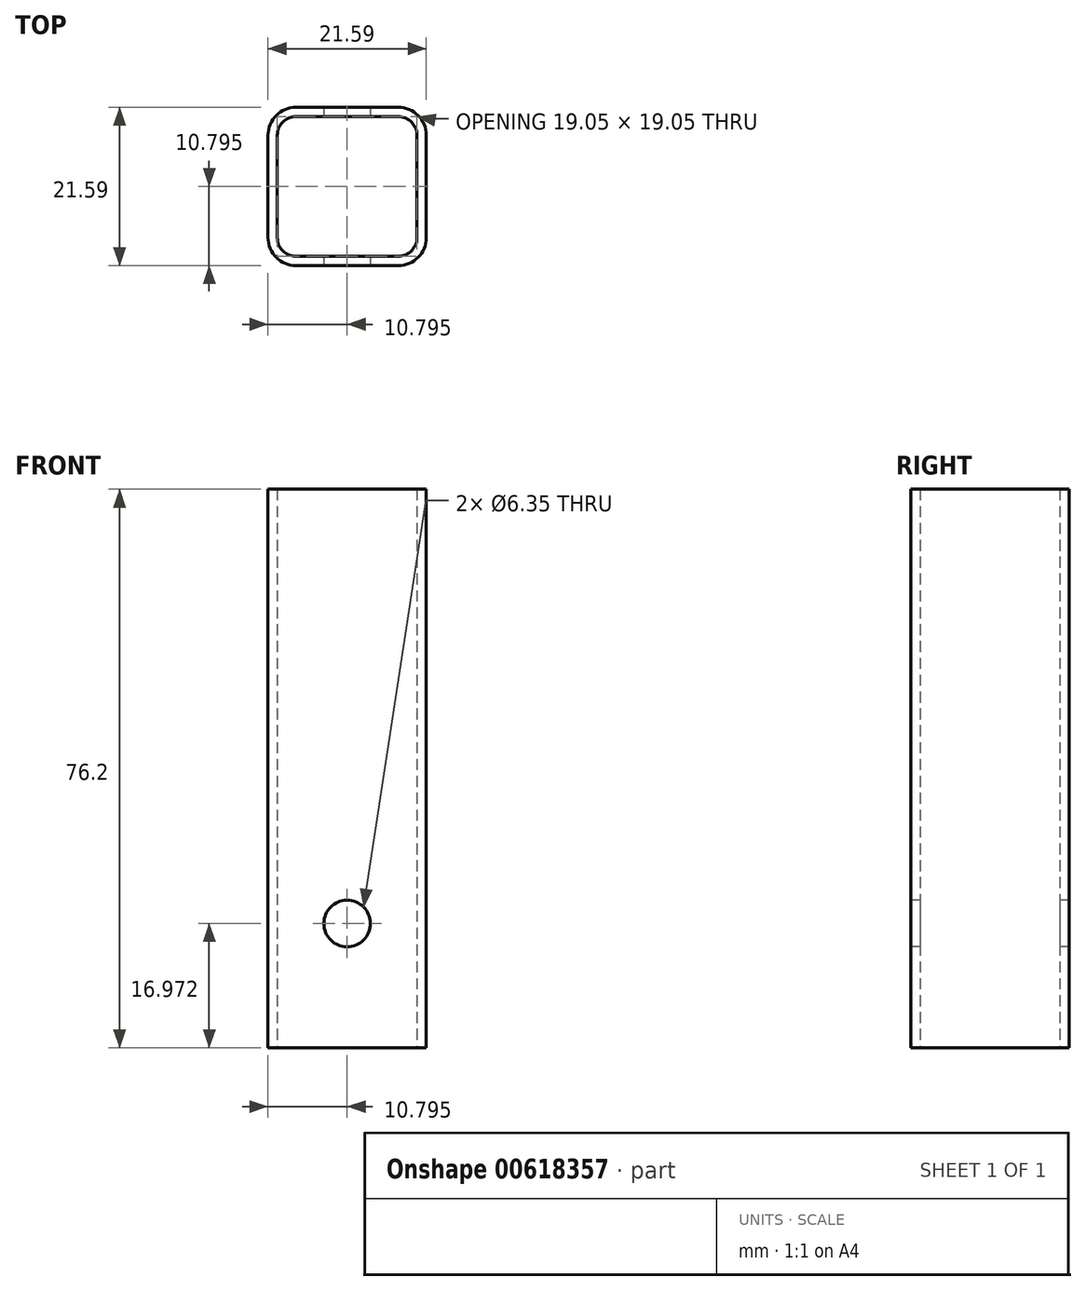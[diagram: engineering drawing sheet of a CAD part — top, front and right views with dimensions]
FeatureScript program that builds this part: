
annotation { "Feature Type Name" : "Feature", "Feature Type Description" : "" }
export const myFeature = defineFeature(function(context is Context, id is Id, definition is map)
    precondition{}
    {
        {
            var Q0;
            Q0=qCreatedBy(makeId("Top.planeOp"),FACE);
            var sketch = newSketch(context, id + "F0", { "sketchPlane" : qUnion([Q0])});
            skLineSegment(sketch, "E0.bottom", {"start": v(2.54, 0) * mm, "end": v(16.51, 0) * mm});
            skLineSegment(sketch, "E0.top", {"start": v(2.54, 19.05) * mm, "end": v(16.5, 19.05) * mm});
            skLineSegment(sketch, "E0.left", {"start": v(0, 2.54) * mm, "end": v(0, 16.5) * mm});
            skLineSegment(sketch, "E0.right", {"start": v(19.05, 2.54) * mm, "end": v(19.05, 16.51) * mm});
            skPoint(sketch, "E1.visualSharp", {"position": v(0, 19.05) * mm});
            skArc(sketch, "E1.filletArc", {"start": v(2.54, 19.05) * mm, "mid": v(0.74, 18.3) * mm, "end": v(0, 16.5) * mm});
            skPoint(sketch, "E2.visualSharp", {"position": v(19.05, 19.05) * mm});
            skArc(sketch, "E2.filletArc", {"start": v(19.05, 16.51) * mm, "mid": v(18.3, 18.3) * mm, "end": v(16.5, 19.05) * mm});
            skPoint(sketch, "E3.visualSharp", {"position": v(19.05, 0) * mm});
            skArc(sketch, "E3.filletArc", {"start": v(16.51, 0) * mm, "mid": v(18.3, 0.74) * mm, "end": v(19.05, 2.54) * mm});
            skPoint(sketch, "E4.visualSharp", {"position": v(0, 0) * mm});
            skArc(sketch, "E4.filletArc", {"start": v(0, 2.54) * mm, "mid": v(0.74, 0.74) * mm, "end": v(2.54, 0) * mm});
            skArc(sketch, "E5.0", {"start": v(2.54, 20.32) * mm, "mid": v(-0.15, 19.2) * mm, "end": v(-1.27, 16.5) * mm});
            skLineSegment(sketch, "E5.1", {"start": v(-1.27, 2.54) * mm, "end": v(-1.27, 16.5) * mm});
            skLineSegment(sketch, "E5.2", {"start": v(2.54, 20.32) * mm, "end": v(16.5, 20.32) * mm});
            skArc(sketch, "E5.3", {"start": v(-1.27, 2.54) * mm, "mid": v(-0.15, -0.15) * mm, "end": v(2.54, -1.27) * mm});
            skArc(sketch, "E5.4", {"start": v(20.32, 16.51) * mm, "mid": v(19.2, 19.2) * mm, "end": v(16.5, 20.32) * mm});
            skLineSegment(sketch, "E5.5", {"start": v(20.32, 2.54) * mm, "end": v(20.32, 16.51) * mm});
            skArc(sketch, "E5.6", {"start": v(16.51, -1.27) * mm, "mid": v(19.2, -0.15) * mm, "end": v(20.32, 2.54) * mm});
            skLineSegment(sketch, "E5.7", {"start": v(2.54, -1.27) * mm, "end": v(16.51, -1.27) * mm});
            skSolve(sketch);
        }
        {
            var Q0;
            Q0=makeQuery(id+"F0.imprint","IMPRINT",FACE,{"disambiguationData":[TD([[makeQuery(id+"F0.imprint","IMPRINT",EDGE,{"derivedFrom":sQuery(id+"F0.wireOp",EDGE,"E0.bottom")}),-1.0]])]});
            var Q1;
            Q1 = qConstructionFilter(qBodyType(qCreatedBy(id + "F0" ,EDGE), BodyType.WIRE), ConstructionObject.NO);
            extrude(context, id + "F1", {"entities" : qUnion([Q0]), "surfaceEntities" : qUnion([Q1]), "depth" : 76.2 * mm, "offsetDistance" : 25.4 * mm});
        }
        {
            var Q0;
            Q0=makeQuery(id+"F1.opExtrude","SWEPT_FACE",FACE,{"disambiguationData":[OSD([sQuery(id+"F0.wireOp",EDGE,"E5.7")])]});
            var sketch = newSketch(context, id + "F2", { "sketchPlane" : qUnion([Q0])});
            skCircle(sketch, "E6", {"center": v(9.53, 16.97) * mm, "radius": 3.18 * mm});
            skPoint(sketch, "E6.centerSnap0", {"position": v(9.53, 76.2) * mm});
            skSolve(sketch);
        }
        {
            var Q0;
            Q0 = qSketchRegion(id + "F2", true);
            extrude(context, id + "F3", {"entities" : qUnion([Q0]), "operationType" : NewBodyOperationType.REMOVE, "endBound" : BoundingType.THROUGH_ALL, "oppositeDirection" : true, "depth" : 25.4 * mm, "offsetDistance" : 25.4 * mm});
        }
    });
